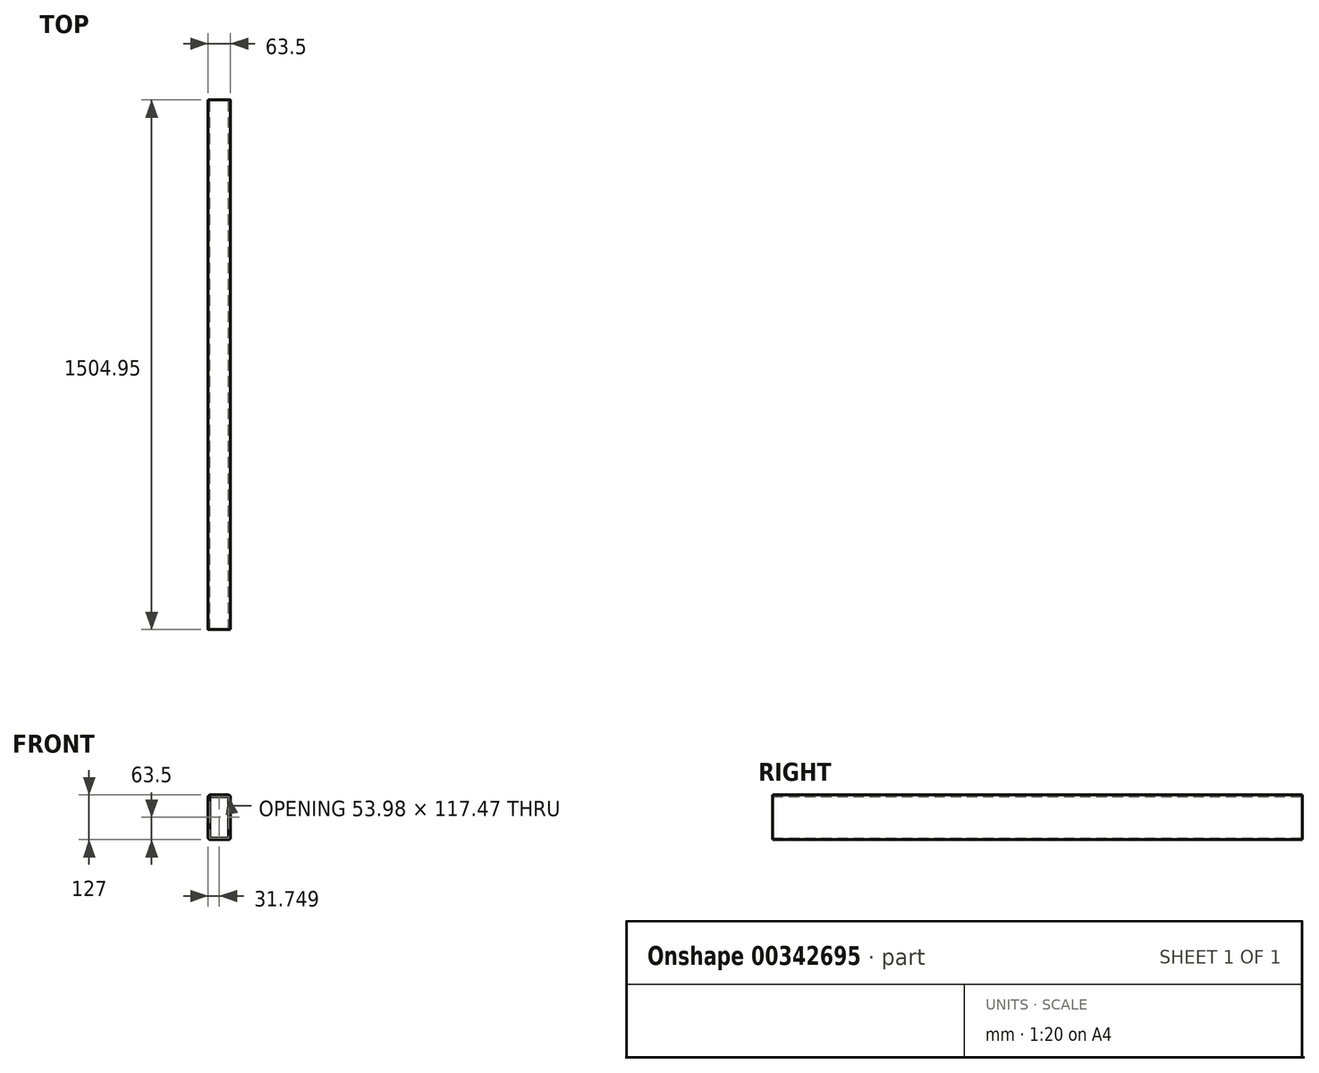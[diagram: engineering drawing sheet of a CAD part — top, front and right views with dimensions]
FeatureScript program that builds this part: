
annotation { "Feature Type Name" : "Feature", "Feature Type Description" : "" }
export const myFeature = defineFeature(function(context is Context, id is Id, definition is map)
    precondition{}
    {
        {
            var Q0;
            Q0=qCreatedBy(makeId("Front.planeOp"),FACE);
            var sketch = newSketch(context, id + "F0", { "sketchPlane" : qUnion([Q0])});
            skLineSegment(sketch, "E0.bottom", {"start": v(23.43, 63.5) * mm, "end": v(-27.37, 63.5) * mm});
            skLineSegment(sketch, "E0.top", {"start": v(23.43, -63.5) * mm, "end": v(-27.37, -63.5) * mm});
            skLineSegment(sketch, "E0.left", {"start": v(29.78, 57.15) * mm, "end": v(29.78, -57.15) * mm});
            skLineSegment(sketch, "E0.right", {"start": v(-33.72, 57.15) * mm, "end": v(-33.72, -57.15) * mm});
            skPoint(sketch, "E0.middle", {"position": v(-1.97, 0) * mm});
            skPoint(sketch, "E1.visualSharp", {"position": v(-33.72, 63.5) * mm});
            skArc(sketch, "E1.filletArc", {"start": v(-27.37, 63.5) * mm, "mid": v(-31.86, 61.64) * mm, "end": v(-33.72, 57.15) * mm});
            skPoint(sketch, "E2.visualSharp", {"position": v(29.78, 63.5) * mm});
            skArc(sketch, "E2.filletArc", {"start": v(29.78, 57.15) * mm, "mid": v(27.92, 61.64) * mm, "end": v(23.43, 63.5) * mm});
            skPoint(sketch, "E3.visualSharp", {"position": v(29.78, -63.5) * mm});
            skArc(sketch, "E3.filletArc", {"start": v(23.43, -63.5) * mm, "mid": v(27.92, -61.64) * mm, "end": v(29.78, -57.15) * mm});
            skPoint(sketch, "E4.visualSharp", {"position": v(-33.72, -63.5) * mm});
            skArc(sketch, "E4.filletArc", {"start": v(-33.72, -57.15) * mm, "mid": v(-31.86, -61.64) * mm, "end": v(-27.37, -63.5) * mm});
            skLineSegment(sketch, "E5.0", {"start": v(25.02, 57.15) * mm, "end": v(25.02, -57.15) * mm});
            skLineSegment(sketch, "E5.1", {"start": v(23.43, 58.74) * mm, "end": v(-27.37, 58.74) * mm});
            skLineSegment(sketch, "E5.2", {"start": v(-28.96, 57.15) * mm, "end": v(-28.96, -57.15) * mm});
            skLineSegment(sketch, "E5.3", {"start": v(23.43, -58.74) * mm, "end": v(-27.37, -58.74) * mm});
            skPoint(sketch, "E6.visualSharp", {"position": v(-28.96, 58.74) * mm});
            skArc(sketch, "E6.filletArc", {"start": v(-27.37, 58.74) * mm, "mid": v(-28.5, 58.27) * mm, "end": v(-28.96, 57.15) * mm});
            skPoint(sketch, "E7.visualSharp", {"position": v(25.02, 58.74) * mm});
            skArc(sketch, "E7.filletArc", {"start": v(25.02, 57.15) * mm, "mid": v(24.55, 58.27) * mm, "end": v(23.43, 58.74) * mm});
            skPoint(sketch, "E8.visualSharp", {"position": v(25.02, -58.74) * mm});
            skArc(sketch, "E8.filletArc", {"start": v(23.43, -58.74) * mm, "mid": v(24.55, -58.27) * mm, "end": v(25.02, -57.15) * mm});
            skPoint(sketch, "E9.visualSharp", {"position": v(-28.96, -58.74) * mm});
            skArc(sketch, "E9.filletArc", {"start": v(-28.96, -57.15) * mm, "mid": v(-28.5, -58.27) * mm, "end": v(-27.37, -58.74) * mm});
            skSolve(sketch);
        }
        {
            var Q0;
            Q0 = qSketchRegion(id + "F0", true);
            extrude(context, id + "F1", {"entities" : qUnion([Q0]), "depth" : 1504.95 * mm});
        }
    });
